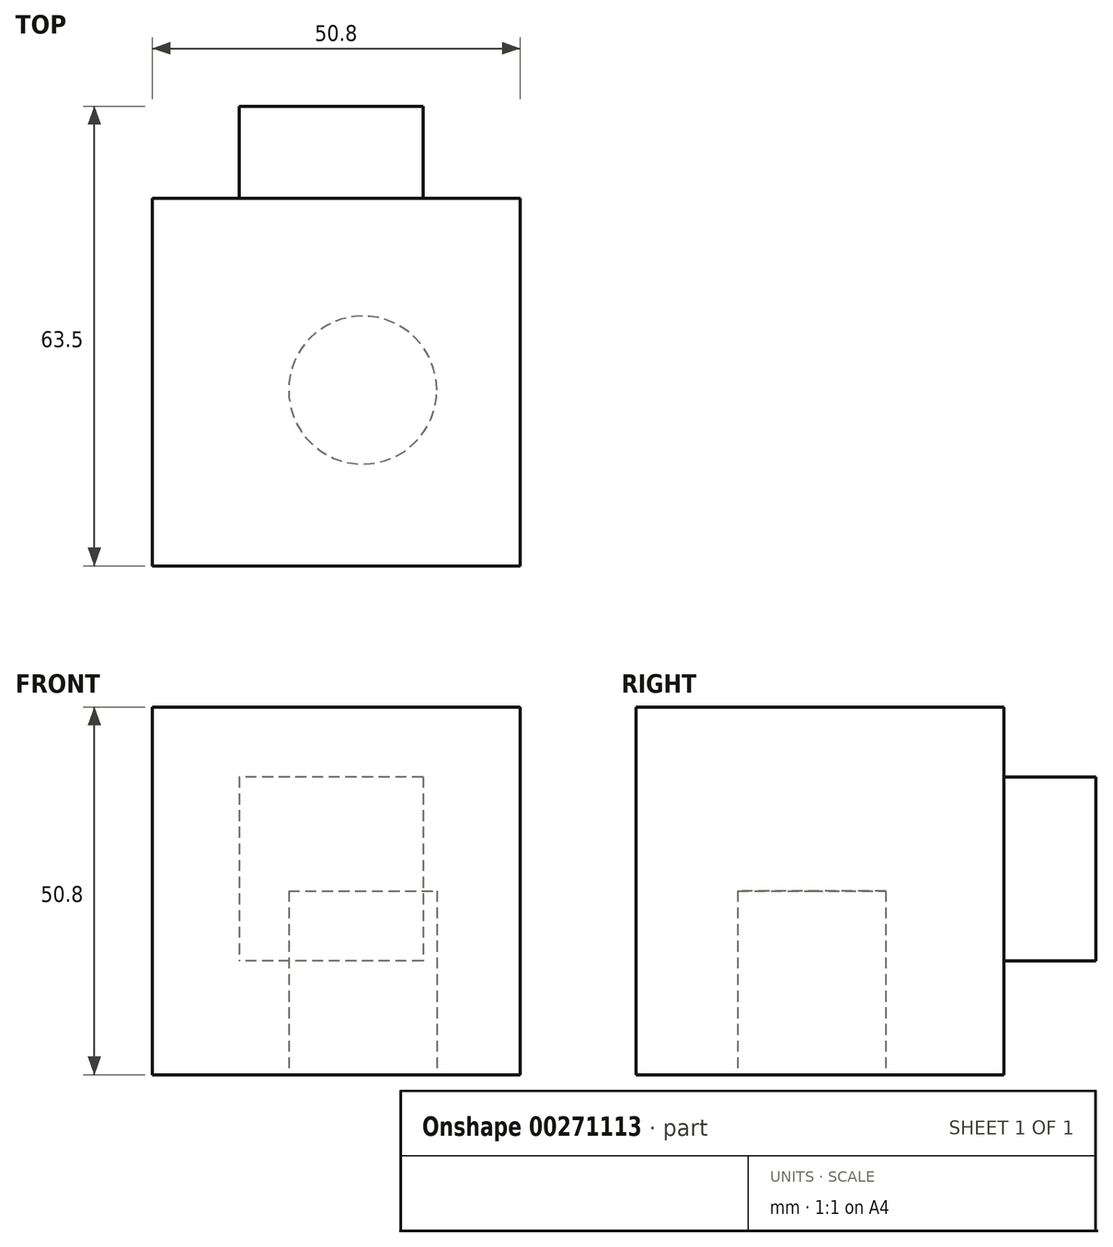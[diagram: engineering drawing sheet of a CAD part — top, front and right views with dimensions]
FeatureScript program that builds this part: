
annotation { "Feature Type Name" : "Feature", "Feature Type Description" : "" }
export const myFeature = defineFeature(function(context is Context, id is Id, definition is map)
    precondition{}
    {
        {
            var Q0;
            Q0=qCreatedBy(makeId("Front.planeOp"),FACE);
            var sketch = newSketch(context, id + "F0", { "sketchPlane" : qUnion([Q0])});
            skLineSegment(sketch, "E0", {"start": v(0, 0) * mm, "end": v(-50.8, 0) * mm});
            skLineSegment(sketch, "E1", {"start": v(-50.8, 0) * mm, "end": v(-50.8, 50.8) * mm});
            skLineSegment(sketch, "E2", {"start": v(-50.8, 50.8) * mm, "end": v(0, 50.8) * mm});
            skLineSegment(sketch, "E3", {"start": v(0, 50.8) * mm, "end": v(0, 0) * mm});
            skSolve(sketch);
        }
        {
            var Q0;
            Q0 = qSketchRegion(id + "F0", true);
            extrude(context, id + "F1", {"entities" : qUnion([Q0]), "depth" : 50.8 * mm});
        }
        {
            var Q0;
            Q0=makeQuery(id+"F1.opExtrude","CAP_FACE",FACE,{"disambiguationData":[OSD([sQuery(id+"F0.wireOp",EDGE,"E0"),sQuery(id+"F0.wireOp",EDGE,"E1"),sQuery(id+"F0.wireOp",EDGE,"E2"),sQuery(id+"F0.wireOp",EDGE,"E3")])],"isStart":true});
            var sketch = newSketch(context, id + "F2", { "sketchPlane" : qUnion([Q0])});
            skLineSegment(sketch, "E4.bottom", {"start": v(13.43, 41.14) * mm, "end": v(38.83, 41.14) * mm});
            skLineSegment(sketch, "E4.top", {"start": v(13.43, 15.74) * mm, "end": v(38.83, 15.74) * mm});
            skLineSegment(sketch, "E4.left", {"start": v(13.43, 41.14) * mm, "end": v(13.43, 15.74) * mm});
            skLineSegment(sketch, "E4.right", {"start": v(38.83, 41.14) * mm, "end": v(38.83, 15.74) * mm});
            skSolve(sketch);
        }
        {
            var Q0;
            Q0=makeQuery(id+"F2.imprint","IMPRINT",FACE,{"disambiguationData":[TD([[makeQuery(id+"F2.imprint","IMPRINT",EDGE,{"derivedFrom":sQuery(id+"F2.wireOp",EDGE,"E4.bottom")}),-1.0]])]});
            extrude(context, id + "F3", {"entities" : qUnion([Q0]), "operationType" : NewBodyOperationType.ADD, "depth" : 12.7 * mm});
        }
        {
            var Q0;
            Q0=makeQuery(id+"F1.opExtrude","SWEPT_FACE",FACE,{"disambiguationData":[OSD([sQuery(id+"F0.wireOp",EDGE,"E0")])]});
            var sketch = newSketch(context, id + "F4", { "sketchPlane" : qUnion([Q0])});
            skCircle(sketch, "E5", {"center": v(-21.74, 26.52) * mm, "radius": 10.22 * mm});
            skSolve(sketch);
        }
        {
            var Q0;
            Q0 = qSketchRegion(id + "F4", true);
            extrude(context, id + "F5", {"entities" : qUnion([Q0]), "operationType" : NewBodyOperationType.REMOVE, "oppositeDirection" : true, "depth" : 25.4 * mm});
        }
    });
